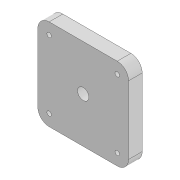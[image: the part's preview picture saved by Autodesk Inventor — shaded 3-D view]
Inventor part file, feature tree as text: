
AUTODESK INVENTOR PART (.ipt)
format: ipt  version: 2020 (Build 240168000, 168)  size: 108,032 bytes
history: native  units: mm
features: other x5, extrude x1
ambient origin geometry x8: Origin, YZ Plane, XZ Plane, XY Plane, X Axis, Y Axis, Z Axis, Center Point
bodies: Body1 (feature_tree)
feature tree (6):
  other  "Sólido1"
  other  "Plano de trabalho1"
  extrude  "Extrusão1"  Depth=10.0mm
  other  "<userpath>\OneDrive\Área de Trabalho\Calorimetro 2022\Inventor\parte_superior.iam"
  other  "parte_superior.iam"
  other  "Corpo_1:4"
